# Revit family: Pavilion Loounge Chair AV5
name_source: partatom
category: Furniture
revit_build: Autodesk Revit 2017 (Build: 20171027_0315(x64)
units: mm (PartAtom-declared; Revit-internal decimal feet)

## family parameters
Always vertical = Yes
Cut with Voids When Loaded = No
OmniClass Number = 23.40.20.00
OmniClass Title = General Furniture and Specialties
Room Calculation Point = No
Shared = No
Work Plane-Based = No

## types (1)
- Pavilion Loounge Chair AV5
    Backcarrier screws = &tradition Powder Coated Steel black
    Backrest = &tradition Lacquered Oak Black Matt Vertical
    Cones = &tradition Powder Coated Steel black
    Depth = 65cm/25.6in
    Description = The Pavilion chair has an airy feeling, with slim arms and legs that give it a light appearance
    Design = Anderssen & Voll
    Design Year = 2018
    Frame = &tradition Powder Coated Steel black
    Gliders = &tradition Plastic Black Matt
    Height = 70cm/27.6in
    Manufacturer = &tradition
    Model = Pavilion Lounge Chair AV5
    Packaging Dimensions = H: 72cm/28.4in, D: 67cm/26.4in, L: 70cm/27.6in
    Seat = &tradition Lacquered Oak Black Matt Horizontal
    Seat Height = 38cm/15.0in
    Type Comments = Pavilion Series
    URL = https://www.andtradition.com
    Variation Backcarrier screws = Satin Polished Brass
    Variation Backrest - Seat = Available in lacquered oak or lacquered walnut
    Variation Glider = Felt Black
    Warranty Period = Two years
    Weight = 5.5kg
    Width = 69cm/27.2in

## geometry (parser evidence)
native form markers: Sweep x1
no freeform markers — native parametric forms only
